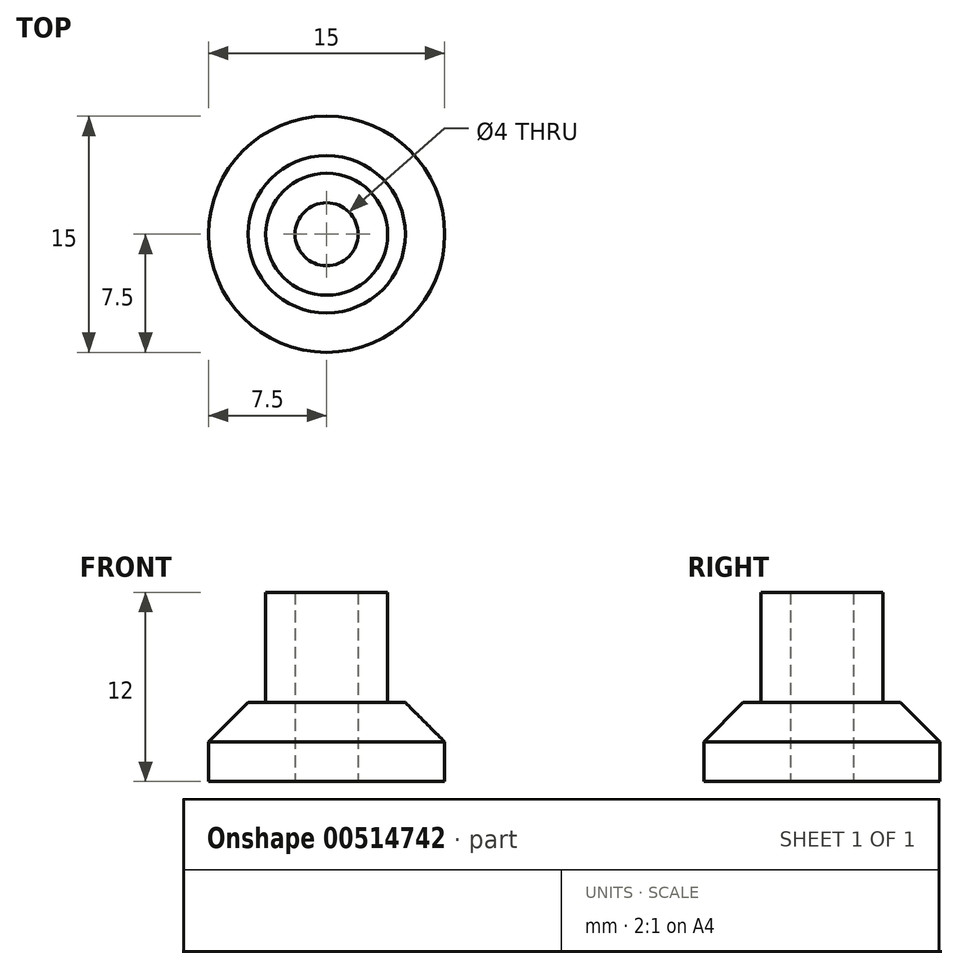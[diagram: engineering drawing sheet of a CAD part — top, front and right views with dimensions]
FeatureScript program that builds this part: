
annotation { "Feature Type Name" : "Feature", "Feature Type Description" : "" }
export const myFeature = defineFeature(function(context is Context, id is Id, definition is map)
    precondition{}
    {
        {
            var Q0;
            Q0=qCreatedBy(makeId("Top.planeOp"),FACE);
            var sketch = newSketch(context, id + "F0", { "sketchPlane" : qUnion([Q0])});
            skCircle(sketch, "E0", {"center": v(0, 0) * mm, "radius": 2 * mm});
            skCircle(sketch, "E1", {"center": v(0, 0) * mm, "radius": 7.5 * mm});
            skSolve(sketch);
        }
        {
            var Q0;
            Q0=makeQuery(id+"F0.imprint","IMPRINT",FACE,{"disambiguationData":[TD([[makeQuery(id+"F0.imprint","IMPRINT",EDGE,{"derivedFrom":sQuery(id+"F0.wireOp",EDGE,"E0")}),-1.0]])]});
            extrude(context, id + "F1", {"entities" : qUnion([Q0]), "depth" : 5 * mm, "offsetDistance" : 25 * mm});
        }
        {
            var Q0;
            Q0=makeQuery(id+"F1.opExtrude","CAP_FACE",FACE,{"disambiguationData":[OSD([sQuery(id+"F0.wireOp",EDGE,"E0"),sQuery(id+"F0.wireOp",EDGE,"E1")])],"isStart":false});
            var sketch = newSketch(context, id + "F2", { "sketchPlane" : qUnion([Q0])});
            skCircle(sketch, "E2", {"center": v(0, 0) * mm, "radius": 2 * mm});
            skCircle(sketch, "E3", {"center": v(0, 0) * mm, "radius": 3.88 * mm});
            skSolve(sketch);
        }
        {
            var Q0;
            Q0=makeQuery(id+"F2.imprint","IMPRINT",FACE,{"disambiguationData":[TD([[makeQuery(id+"F2.imprint","IMPRINT",EDGE,{"derivedFrom":sQuery(id+"F2.wireOp",EDGE,"E2")}),-1.0]])]});
            extrude(context, id + "F3", {"entities" : qUnion([Q0]), "operationType" : NewBodyOperationType.ADD, "depth" : 7 * mm, "offsetDistance" : 25 * mm});
        }
        {
            var Q0;
            Q0=makeQuery(id+"F1.opExtrude","CAP_EDGE",EDGE,{"disambiguationData":[OSD([sQuery(id+"F0.wireOp",EDGE,"E1")])],"isStart":false});
            chamfer(context, id + "F4", {"entities" : qUnion([Q0]), "width" : 2.5 * mm, "tangentPropagation" : true});
        }
    });
